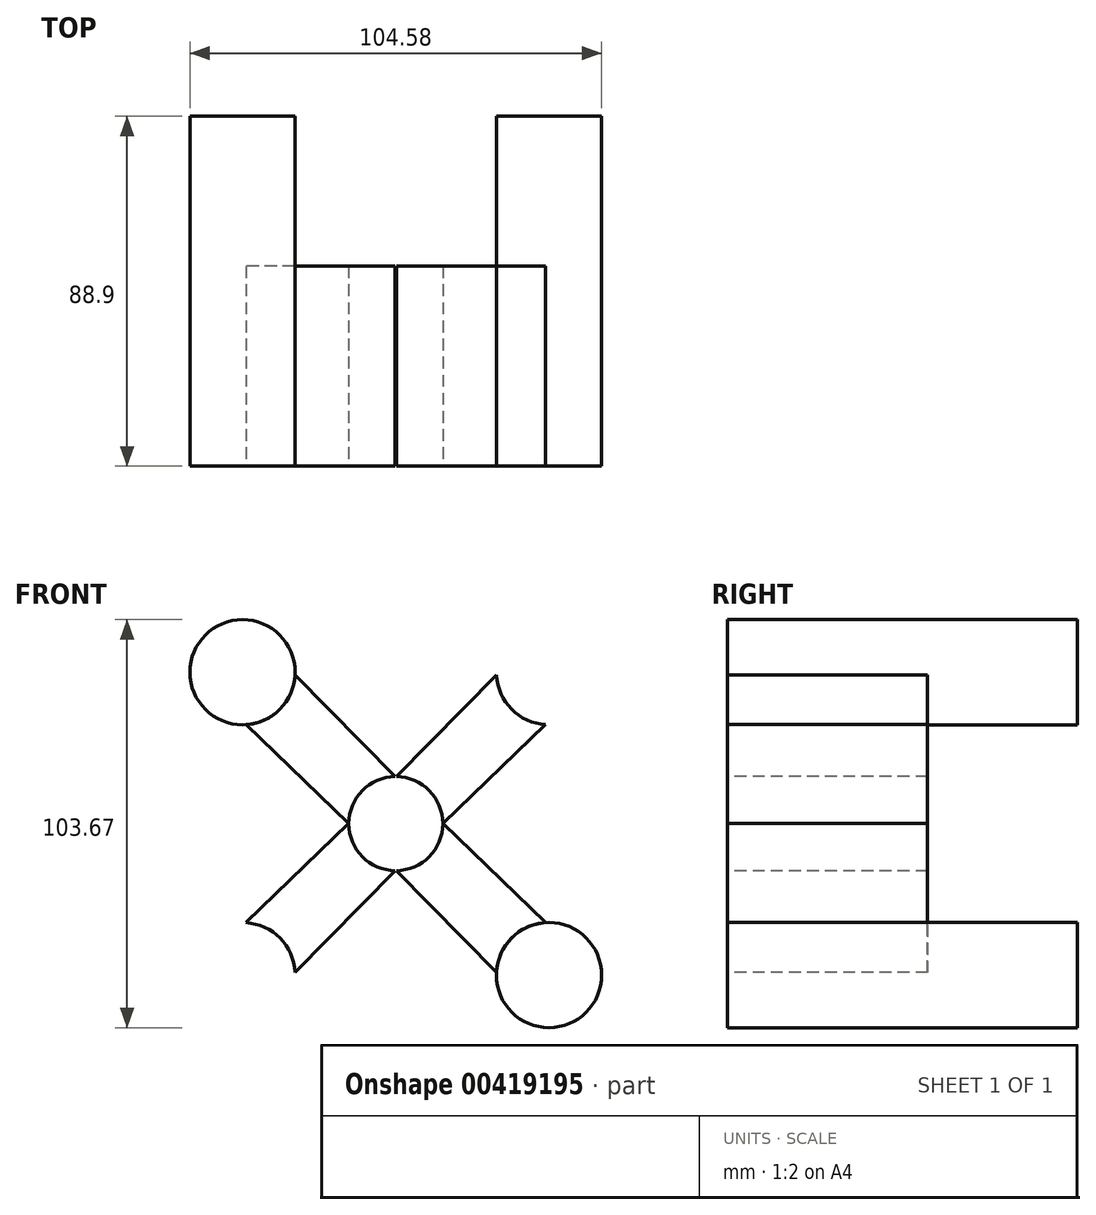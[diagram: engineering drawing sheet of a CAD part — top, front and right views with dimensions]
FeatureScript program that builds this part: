
annotation { "Feature Type Name" : "Feature", "Feature Type Description" : "" }
export const myFeature = defineFeature(function(context is Context, id is Id, definition is map)
    precondition{}
    {
        {
            var Q0;
            Q0=qCreatedBy(makeId("Front.planeOp"),FACE);
            var sketch = newSketch(context, id + "F0", { "sketchPlane" : qUnion([Q0])});
            skCircle(sketch, "E0", {"center": v(50.03, 6.68) * mm, "radius": 11.95 * mm});
            skLineSegment(sketch, "E1", {"start": v(50.03, 6.68) * mm, "end": v(11.1, 45.16) * mm, "construction": true});
            skCircle(sketch, "E2", {"center": v(11.1, 45.16) * mm, "radius": 13.36 * mm});
            skLineSegment(sketch, "E3", {"start": v(38.08, 6.68) * mm, "end": v(11.99, 31.83) * mm});
            skLineSegment(sketch, "E4.MirrorCS", {"start": v(61.98, 6.68) * mm, "end": v(88.07, 31.83) * mm});
            skLineSegment(sketch, "E5.MirrorCS", {"start": v(49.89, 18.64) * mm, "end": v(24.44, 44.43) * mm});
            skLineSegment(sketch, "E6.MirrorCS", {"start": v(50.17, 18.64) * mm, "end": v(75.62, 44.43) * mm});
            skCircle(sketch, "E7.MirrorC", {"center": v(88.96, 45.16) * mm, "radius": 13.36 * mm});
            skLineSegment(sketch, "E8.MirrorCS", {"start": v(50.17, -5.27) * mm, "end": v(75.62, -31.06) * mm});
            skCircle(sketch, "E9.MirrorC", {"center": v(88.96, -31.8) * mm, "radius": 13.36 * mm});
            skLineSegment(sketch, "E10.MirrorCS", {"start": v(61.98, 6.68) * mm, "end": v(88.07, -18.46) * mm});
            skLineSegment(sketch, "E11.MirrorCS", {"start": v(49.89, -5.27) * mm, "end": v(24.44, -31.06) * mm});
            skLineSegment(sketch, "E12.MirrorCS", {"start": v(38.08, 6.68) * mm, "end": v(11.99, -18.46) * mm});
            skCircle(sketch, "E13.MirrorC", {"center": v(11.1, -31.8) * mm, "radius": 13.36 * mm});
            skSolve(sketch);
        }
        {
            var Q0;
            {var subQ0=sQuery(id+"F0.wireOp",EDGE,"E7.MirrorC");var subQ1=makeQuery(id+"F0.imprint","INTERSECT",VERTEX,{"derivedFrom":[sQuery(id+"F0.wireOp",EDGE,"E4.MirrorCS"),subQ0]});Q0=makeQuery(id+"F0.imprint","IMPRINT",FACE,{"disambiguationData":[TD([[makeQuery(id+"F0.imprint","IMPRINT",EDGE,{"disambiguationData":[TD([[subQ1,-1.0]])],"derivedFrom":subQ0}),-1.0]])]});}
            var Q1;
            {var subQ0=sQuery(id+"F0.wireOp",EDGE,"E2");var subQ1=makeQuery(id+"F0.imprint","INTERSECT",VERTEX,{"derivedFrom":[subQ0,sQuery(id+"F0.wireOp",EDGE,"E3")]});Q1=makeQuery(id+"F0.imprint","IMPRINT",FACE,{"disambiguationData":[TD([[makeQuery(id+"F0.imprint","IMPRINT",EDGE,{"disambiguationData":[TD([[subQ1,-1.0]])],"derivedFrom":subQ0}),1.0]])]});}
            var Q2;
            {var subQ0=sQuery(id+"F0.wireOp",EDGE,"E13.MirrorC");var subQ1=makeQuery(id+"F0.imprint","INTERSECT",VERTEX,{"derivedFrom":[sQuery(id+"F0.wireOp",EDGE,"E11.MirrorCS"),subQ0]});Q2=makeQuery(id+"F0.imprint","IMPRINT",FACE,{"disambiguationData":[TD([[makeQuery(id+"F0.imprint","IMPRINT",EDGE,{"disambiguationData":[TD([[subQ1,1.0]])],"derivedFrom":subQ0}),-1.0]])]});}
            var Q3;
            {var subQ0=sQuery(id+"F0.wireOp",EDGE,"E9.MirrorC");var subQ1=makeQuery(id+"F0.imprint","INTERSECT",VERTEX,{"derivedFrom":[sQuery(id+"F0.wireOp",EDGE,"E8.MirrorCS"),subQ0]});Q3=makeQuery(id+"F0.imprint","IMPRINT",FACE,{"disambiguationData":[TD([[makeQuery(id+"F0.imprint","IMPRINT",EDGE,{"disambiguationData":[TD([[subQ1,1.0]])],"derivedFrom":subQ0}),1.0]])]});}
            extrude(context, id + "F1", {"entities" : qUnion([Q0, Q1, Q2, Q3]), "depth" : -88.9 * mm});
        }
        {
            var Q0;
            {var subQ0=sQuery(id+"F0.wireOp",EDGE,"E4.MirrorCS");Q0=makeQuery(id+"F0.imprint","IMPRINT",FACE,{"disambiguationData":[TD([[makeQuery(id+"F0.imprint","IMPRINT",EDGE,{"derivedFrom":subQ0}),1.0]])]});}
            var Q1;
            {var subQ2=sQuery(id+"F0.wireOp",EDGE,"E8.MirrorCS");Q1=makeQuery(id+"F0.imprint","IMPRINT",FACE,{"disambiguationData":[TD([[makeQuery(id+"F0.imprint","IMPRINT",EDGE,{"derivedFrom":subQ2}),1.0]])]});}
            var Q2;
            {var subQ2=sQuery(id+"F0.wireOp",EDGE,"E11.MirrorCS");Q2=makeQuery(id+"F0.imprint","IMPRINT",FACE,{"disambiguationData":[TD([[makeQuery(id+"F0.imprint","IMPRINT",EDGE,{"derivedFrom":subQ2}),-1.0]])]});}
            var Q3;
            {var subQ0=sQuery(id+"F0.wireOp",EDGE,"E3");Q3=makeQuery(id+"F0.imprint","IMPRINT",FACE,{"disambiguationData":[TD([[makeQuery(id+"F0.imprint","IMPRINT",EDGE,{"derivedFrom":subQ0}),-1.0]])]});}
            extrude(context, id + "F2", {"entities" : qUnion([Q0, Q1, Q2, Q3]), "depth" : -50.8 * mm});
        }
    });
